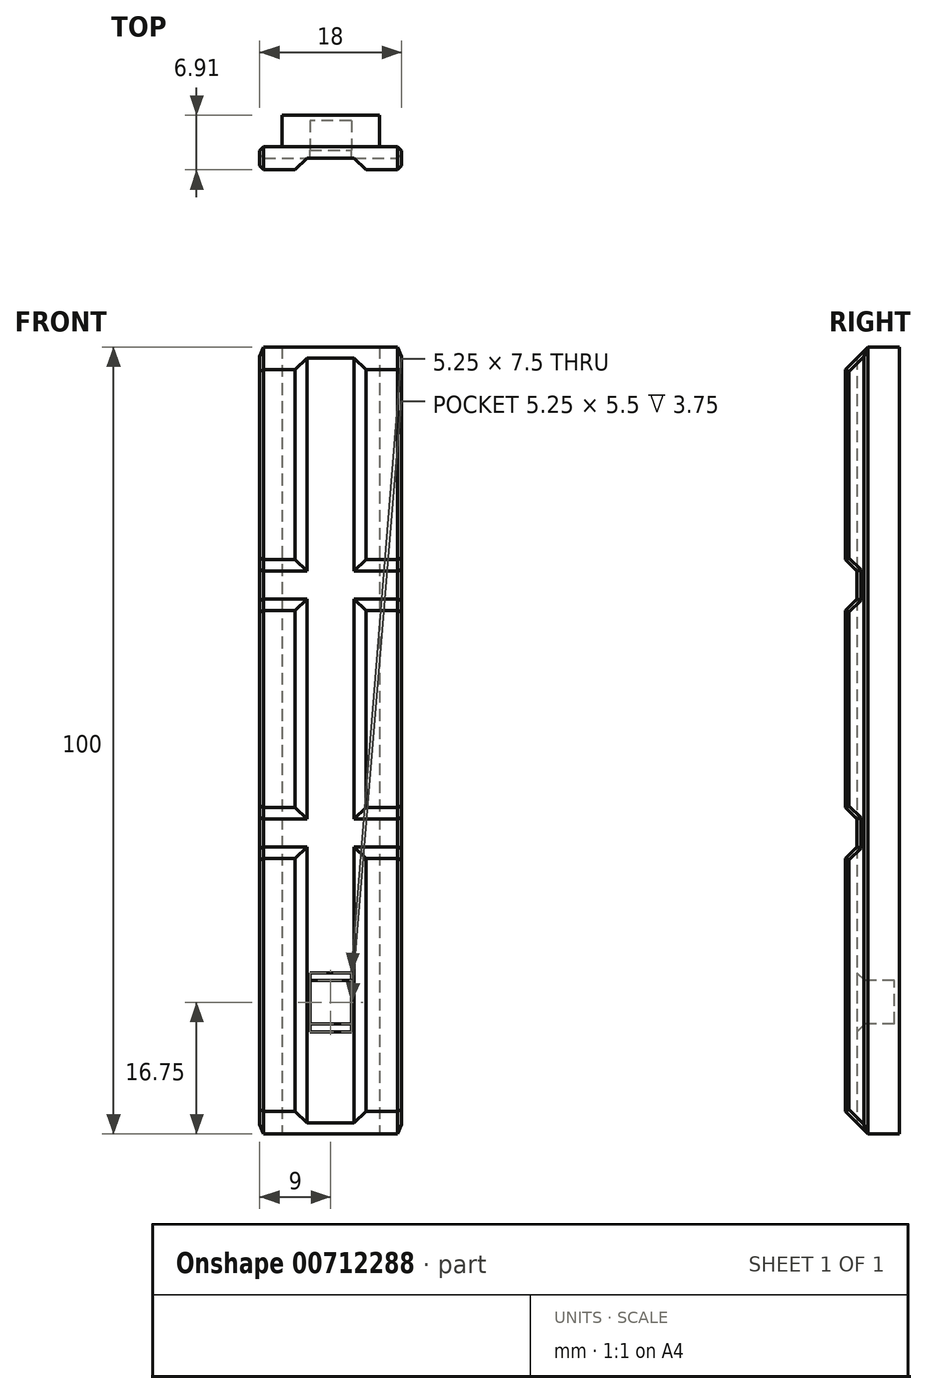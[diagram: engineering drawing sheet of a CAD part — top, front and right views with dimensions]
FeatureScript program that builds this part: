
annotation { "Feature Type Name" : "Feature", "Feature Type Description" : "" }
export const myFeature = defineFeature(function(context is Context, id is Id, definition is map)
    precondition{}
    {
        {
            var Q0;
            Q0=qCreatedBy(makeId("Top.planeOp"),FACE);
            var sketch = newSketch(context, id + "F0", { "sketchPlane" : qUnion([Q0])});
            skLineSegment(sketch, "E0", {"start": v(0, 0) * mm, "end": v(0, 2.91) * mm});
            skLineSegment(sketch, "E1", {"start": v(0, 2.91) * mm, "end": v(2.8, 2.91) * mm});
            skLineSegment(sketch, "E2", {"start": v(18, 0) * mm, "end": v(18, 2.91) * mm});
            skLineSegment(sketch, "E3", {"start": v(18, 2.91) * mm, "end": v(15.2, 2.91) * mm});
            skLineSegment(sketch, "E4", {"start": v(2.8, 2.91) * mm, "end": v(2.8, 6.9) * mm});
            skLineSegment(sketch, "E5", {"start": v(15.2, 2.91) * mm, "end": v(15.2, 6.9) * mm});
            skLineSegment(sketch, "E6", {"start": v(0, 0) * mm, "end": v(4.5, 0) * mm});
            skLineSegment(sketch, "E7", {"start": v(4.5, 0) * mm, "end": v(6, 1.5) * mm});
            skLineSegment(sketch, "E8", {"start": v(2.8, 6.9) * mm, "end": v(15.2, 6.9) * mm});
            skLineSegment(sketch, "E9", {"start": v(18, 0) * mm, "end": v(13.5, 0) * mm});
            skLineSegment(sketch, "E10", {"start": v(12, 1.5) * mm, "end": v(13.5, 0) * mm});
            skLineSegment(sketch, "E11", {"start": v(6, 1.5) * mm, "end": v(12, 1.5) * mm});
            skSolve(sketch);
        }
        {
            var Q0;
            Q0 = qSketchRegion(id + "F0", true);
            extrude(context, id + "F1", {"entities" : qUnion([Q0]), "depth" : 100 * mm, "offsetDistance" : 25 * mm});
        }
        {
            var Q0;
            Q0=qCreatedBy(makeId("Right.planeOp"),FACE);
            var sketch = newSketch(context, id + "F2", { "sketchPlane" : qUnion([Q0])});
            skLineSegment(sketch, "E12", {"start": v(0, 0) * mm, "end": v(0, 35) * mm});
            skLineSegment(sketch, "E13", {"start": v(1.5, 35) * mm, "end": v(1.5, 41.5) * mm});
            skLineSegment(sketch, "E14", {"start": v(0, 41.5) * mm, "end": v(0, 66.5) * mm});
            skLineSegment(sketch, "E15", {"start": v(1.5, 41.5) * mm, "end": v(1.5, 40) * mm});
            skLineSegment(sketch, "E16", {"start": v(0, 41.5) * mm, "end": v(1.5, 40) * mm});
            skLineSegment(sketch, "E17", {"start": v(1.5, 35) * mm, "end": v(1.5, 36.5) * mm});
            skLineSegment(sketch, "E18", {"start": v(1.5, 36.5) * mm, "end": v(0, 35) * mm});
            skLineSegment(sketch, "E19", {"start": v(0, 66.5) * mm, "end": v(1.5, 68) * mm});
            skLineSegment(sketch, "E20", {"start": v(1.5, 66.5) * mm, "end": v(1.5, 73) * mm});
            skLineSegment(sketch, "E21", {"start": v(0, 73) * mm, "end": v(1.5, 71.5) * mm});
            skLineSegment(sketch, "E22", {"start": v(0, 73) * mm, "end": v(0, 100) * mm});
            skLineSegment(sketch, "E23", {"start": v(0, 100) * mm, "end": v(-0.98, 100) * mm});
            skLineSegment(sketch, "E24", {"start": v(-0.98, 100) * mm, "end": v(-0.98, 0) * mm});
            skLineSegment(sketch, "E25", {"start": v(-0.98, 0) * mm, "end": v(0, 0) * mm});
            skSolve(sketch);
        }
        {
            var Q0;
            Q0 = qSketchRegion(id + "F2", true);
            extrude(context, id + "F3", {"entities" : qUnion([Q0]), "operationType" : NewBodyOperationType.REMOVE, "oppositeDirection" : true, "depth" : 25 * mm, "offsetDistance" : 25 * mm, "hasSecondDirection" : true, "secondDirectionOppositeDirection" : false, "secondDirectionDepth" : 25 * mm});
        }
        {
            var Q0;
            Q0=makeQuery(id+"F1.opExtrude","CAP_EDGE",EDGE,{"disambiguationData":[OSD([sQuery(id+"F0.wireOp",EDGE,"E6")])],"isStart":true});
            chamfer(context, id + "F4", {"entities" : qUnion([Q0]), "width" : 2.91 * mm, "tangentPropagation" : true});
        }
        {
            var Q0;
            Q0=makeQuery(id+"F1.opExtrude","CAP_EDGE",EDGE,{"disambiguationData":[OSD([sQuery(id+"F0.wireOp",EDGE,"E9")])],"isStart":false});
            chamfer(context, id + "F5", {"entities" : qUnion([Q0]), "width" : 2.91 * mm, "tangentPropagation" : true});
        }
        {
            var Q0;
            Q0=qCreatedBy(makeId("Front.planeOp"),FACE);
            var sketch = newSketch(context, id + "F6", { "sketchPlane" : qUnion([Q0])});
            skLineSegment(sketch, "E26", {"start": v(0, 0) * mm, "end": v(9, 0) * mm});
            skLineSegment(sketch, "E27", {"start": v(9, 0) * mm, "end": v(9, 14) * mm});
            skLineSegment(sketch, "E28", {"start": v(9, 14) * mm, "end": v(11.63, 14) * mm});
            skLineSegment(sketch, "E29", {"start": v(9, 14) * mm, "end": v(6.38, 14) * mm});
            skLineSegment(sketch, "E30", {"start": v(6.38, 14) * mm, "end": v(6.38, 19.5) * mm});
            skLineSegment(sketch, "E31", {"start": v(11.63, 14) * mm, "end": v(11.63, 19.5) * mm});
            skLineSegment(sketch, "E32", {"start": v(6.38, 19.5) * mm, "end": v(11.63, 19.5) * mm});
            skSolve(sketch);
        }
        {
            var Q0;
            Q0=makeQuery(id+"F6.imprint","IMPRINT",FACE,{"disambiguationData":[TD([[makeQuery(id+"F6.imprint","IMPRINT",EDGE,{"derivedFrom":sQuery(id+"F6.wireOp",EDGE,"E28")}),1.0]])]});
            extrude(context, id + "F7", {"entities" : qUnion([Q0]), "operationType" : NewBodyOperationType.REMOVE, "oppositeDirection" : true, "depth" : 6.25 * mm, "offsetDistance" : 25 * mm});
        }
        {
            var Q0;
            Q0=makeQuery(id+"F7.boolean.opBoolean","INTERSECT",EDGE,{"derivedFrom":[makeQuery(id+"F3.boolean.opBoolean","MERGE",FACE,{"derivedFrom":[makeQuery(id+"F1.opExtrude","SWEPT_FACE",FACE,{"disambiguationData":[OSD([sQuery(id+"F0.wireOp",EDGE,"E11")])]}),makeQuery(id+"F3.opExtrude","SWEPT_FACE",FACE,{"disambiguationData":[OSD([sQuery(id+"F2.wireOp",EDGE,"E13")])]}),makeQuery(id+"F3.opExtrude","SWEPT_FACE",FACE,{"disambiguationData":[OSD([sQuery(id+"F2.wireOp",EDGE,"E20")])]})]}),makeQuery(id+"F7.opExtrude","SWEPT_FACE",FACE,{"disambiguationData":[OSD([sQuery(id+"F6.wireOp",EDGE,"E28"),sQuery(id+"F6.wireOp",EDGE,"E29")])]})]});
            var Q1;
            Q1=makeQuery(id+"F7.boolean.opBoolean","INTERSECT",EDGE,{"derivedFrom":[makeQuery(id+"F3.boolean.opBoolean","MERGE",FACE,{"derivedFrom":[makeQuery(id+"F1.opExtrude","SWEPT_FACE",FACE,{"disambiguationData":[OSD([sQuery(id+"F0.wireOp",EDGE,"E11")])]}),makeQuery(id+"F3.opExtrude","SWEPT_FACE",FACE,{"disambiguationData":[OSD([sQuery(id+"F2.wireOp",EDGE,"E13")])]}),makeQuery(id+"F3.opExtrude","SWEPT_FACE",FACE,{"disambiguationData":[OSD([sQuery(id+"F2.wireOp",EDGE,"E20")])]})]}),makeQuery(id+"F7.opExtrude","SWEPT_FACE",FACE,{"disambiguationData":[OSD([sQuery(id+"F6.wireOp",EDGE,"E32")])]})]});
            chamfer(context, id + "F8", {"entities" : qUnion([Q0, Q1]), "width" : 1 * mm, "tangentPropagation" : true});
        }
        {
            var Q0;
            Q0=makeQuery(id+"F1.opExtrude","SWEPT_FACE",FACE,{"disambiguationData":[OSD([sQuery(id+"F0.wireOp",EDGE,"E2")])]});
            var Q1;
            Q1=makeQuery(id+"F1.opExtrude","SWEPT_FACE",FACE,{"disambiguationData":[OSD([sQuery(id+"F0.wireOp",EDGE,"E0")])]});
            chamfer(context, id + "F9", {"entities" : qUnion([Q0, Q1]), "width" : 0.5 * mm, "tangentPropagation" : true});
        }
    });
